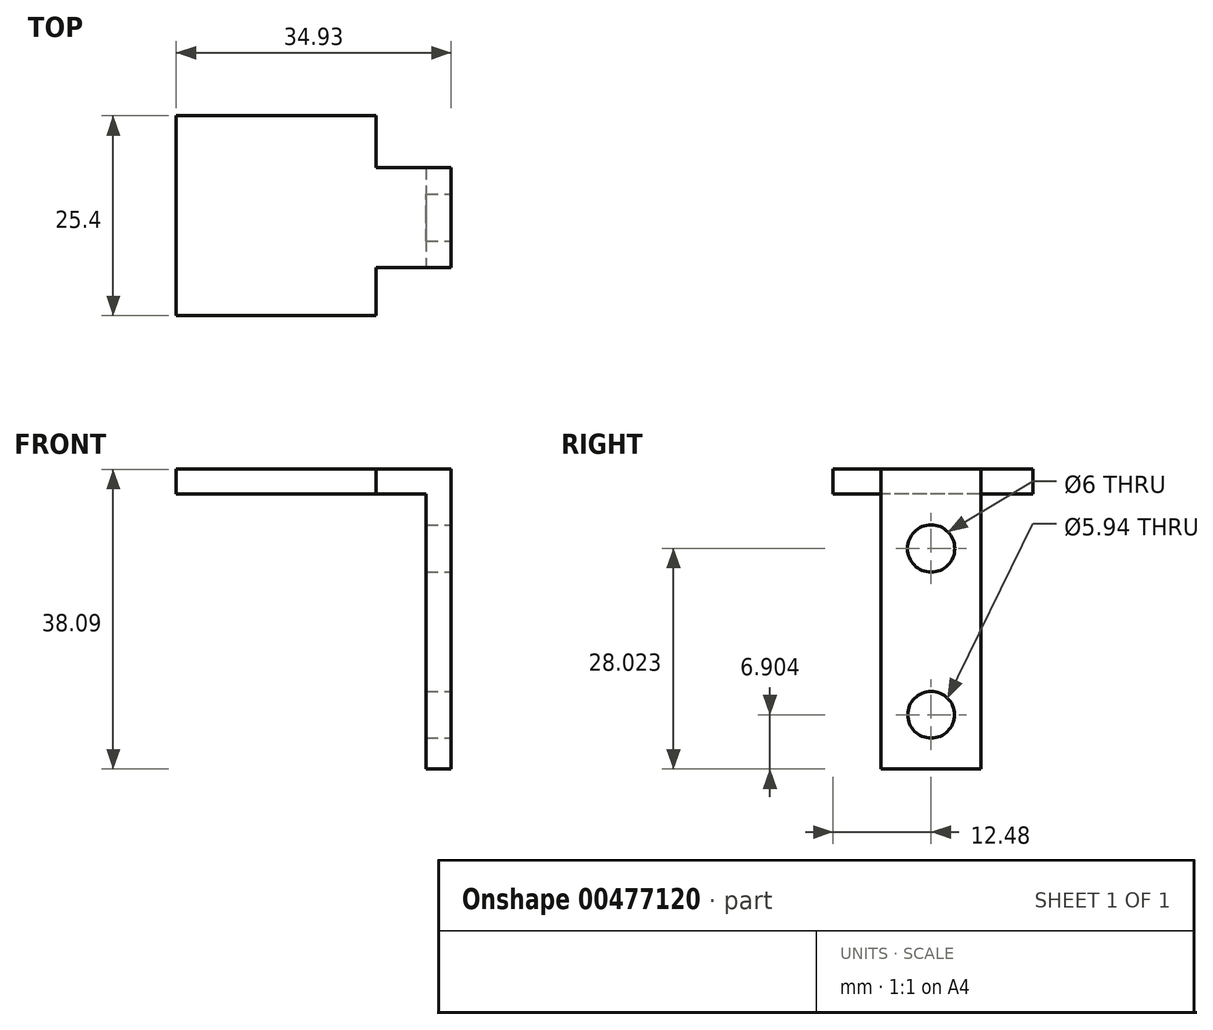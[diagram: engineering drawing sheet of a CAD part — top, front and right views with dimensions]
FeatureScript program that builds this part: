
annotation { "Feature Type Name" : "Feature", "Feature Type Description" : "" }
export const myFeature = defineFeature(function(context is Context, id is Id, definition is map)
    precondition{}
    {
        {
            var Q0;
            Q0=qCreatedBy(makeId("Top.planeOp"),FACE);
            var sketch = newSketch(context, id + "F0", { "sketchPlane" : qUnion([Q0])});
            skLineSegment(sketch, "E0.bottom", {"start": v(-11.79, 6.57) * mm, "end": v(13.61, 6.57) * mm});
            skLineSegment(sketch, "E0.top", {"start": v(-11.79, -18.83) * mm, "end": v(13.61, -18.83) * mm});
            skLineSegment(sketch, "E0.left", {"start": v(-11.79, 6.57) * mm, "end": v(-11.79, -18.83) * mm});
            skLineSegment(sketch, "E0.right", {"start": v(13.61, 6.57) * mm, "end": v(13.61, -18.83) * mm});
            skSolve(sketch);
        }
        {
            var Q0;
            Q0=qSketchRegion(id+"F0",true);
            extrude(context, id + "F1", {"entities" : qUnion([Q0]), "depth" : 3.17 * mm});
        }
        {
            var Q0;
            Q0=makeQuery(id+"F1.opExtrude","SWEPT_FACE",FACE,{"disambiguationData":[OSD([sQuery(id+"F0.wireOp",EDGE,"E0.right")])]});
            var sketch = newSketch(context, id + "F2", { "sketchPlane" : qUnion([Q0])});
            skLineSegment(sketch, "E1.bottom", {"start": v(0, 3.18) * mm, "end": v(-12.7, 3.18) * mm});
            skLineSegment(sketch, "E1.top", {"start": v(0, 0) * mm, "end": v(-12.7, 0) * mm});
            skLineSegment(sketch, "E1.left", {"start": v(0, 3.18) * mm, "end": v(0, 0) * mm});
            skLineSegment(sketch, "E1.right", {"start": v(-12.7, 3.17) * mm, "end": v(-12.7, 0) * mm});
            skSolve(sketch);
        }
        {
            var Q0;
            Q0=qSketchRegion(id+"F2",true);
            extrude(context, id + "F3", {"entities" : qUnion([Q0]), "operationType" : NewBodyOperationType.ADD, "depth" : 6.35 * mm});
        }
        {
            var Q0;
            Q0=makeQuery(id+"F3.opExtrude","CAP_FACE",FACE,{"disambiguationData":[OSD([sQuery(id+"F2.wireOp",EDGE,"E1.bottom"),sQuery(id+"F2.wireOp",EDGE,"E1.top"),sQuery(id+"F2.wireOp",EDGE,"E1.left"),sQuery(id+"F2.wireOp",EDGE,"E1.right")])],"isStart":false});
            var sketch = newSketch(context, id + "F4", { "sketchPlane" : qUnion([Q0])});
            skLineSegment(sketch, "E2.bottom", {"start": v(-12.7, 3.18) * mm, "end": v(0, 3.18) * mm});
            skLineSegment(sketch, "E2.top", {"start": v(-12.7, -34.93) * mm, "end": v(0, -34.93) * mm});
            skLineSegment(sketch, "E2.left", {"start": v(-12.7, 3.17) * mm, "end": v(-12.7, -34.93) * mm});
            skLineSegment(sketch, "E2.right", {"start": v(0, 3.17) * mm, "end": v(0, -34.93) * mm});
            skSolve(sketch);
        }
        {
            var Q0;
            Q0=qSketchRegion(id+"F4",true);
            extrude(context, id + "F5", {"entities" : qUnion([Q0]), "operationType" : NewBodyOperationType.ADD, "depth" : 3.17 * mm});
        }
        {
            var Q0;
            Q0=makeQuery(id+"F5.opExtrude","CAP_FACE",FACE,{"disambiguationData":[OSD([sQuery(id+"F4.wireOp",EDGE,"E2.bottom"),sQuery(id+"F4.wireOp",EDGE,"E2.top"),sQuery(id+"F4.wireOp",EDGE,"E2.left"),sQuery(id+"F4.wireOp",EDGE,"E2.right")])],"isStart":false});
            var sketch = newSketch(context, id + "F6", { "sketchPlane" : qUnion([Q0])});
            skCircle(sketch, "E3", {"center": v(-6.35, -6.9) * mm, "radius": 3 * mm});
            skPoint(sketch, "E3.centerSnap0", {"position": v(-6.35, 3.18) * mm});
            skSolve(sketch);
        }
        {
            var Q0;
            Q0=makeQuery(id+"F6.imprint","IMPRINT",FACE,{"disambiguationData":[TD([[makeQuery(id+"F6.imprint","IMPRINT",EDGE,{"derivedFrom":sQuery(id+"F6.wireOp",EDGE,"E3")}),1.0]])]});
            extrude(context, id + "F7", {"entities" : qUnion([Q0]), "operationType" : NewBodyOperationType.REMOVE, "oppositeDirection" : true, "depth" : 3.2 * mm});
        }
        {
            var Q0;
            Q0=makeQuery(id+"F5.opExtrude","CAP_FACE",FACE,{"disambiguationData":[OSD([sQuery(id+"F4.wireOp",EDGE,"E2.bottom"),sQuery(id+"F4.wireOp",EDGE,"E2.top"),sQuery(id+"F4.wireOp",EDGE,"E2.left"),sQuery(id+"F4.wireOp",EDGE,"E2.right")])],"isStart":false});
            var sketch = newSketch(context, id + "F8", { "sketchPlane" : qUnion([Q0])});
            skCircle(sketch, "E4", {"center": v(-6.35, -28.02) * mm, "radius": 2.97 * mm});
            skPoint(sketch, "E4.centerSnap0", {"position": v(-6.35, 3.18) * mm});
            skSolve(sketch);
        }
        {
            var Q0;
            Q0=makeQuery(id+"F8.imprint","IMPRINT",FACE,{"disambiguationData":[TD([[makeQuery(id+"F8.imprint","IMPRINT",EDGE,{"derivedFrom":sQuery(id+"F8.wireOp",EDGE,"E4")}),1.0]])]});
            var sketch = newSketch(context, id + "F9", { "sketchPlane" : qUnion([Q0])});
            skSolve(sketch);
        }
        {
            var Q0;
            Q0=makeQuery(id+"F9.imprint","IMPRINT",FACE,{"disambiguationData":[TD([[makeQuery(id+"F9.imprint","IMPRINT",EDGE,{"derivedFrom":makeQuery(id+"F8.imprint","IMPRINT",EDGE,{"derivedFrom":sQuery(id+"F8.wireOp",EDGE,"E4")})}),1.0]])]});
            extrude(context, id + "F10", {"entities" : qUnion([Q0]), "operationType" : NewBodyOperationType.REMOVE, "oppositeDirection" : true, "depth" : 3.17 * mm});
        }
    });
